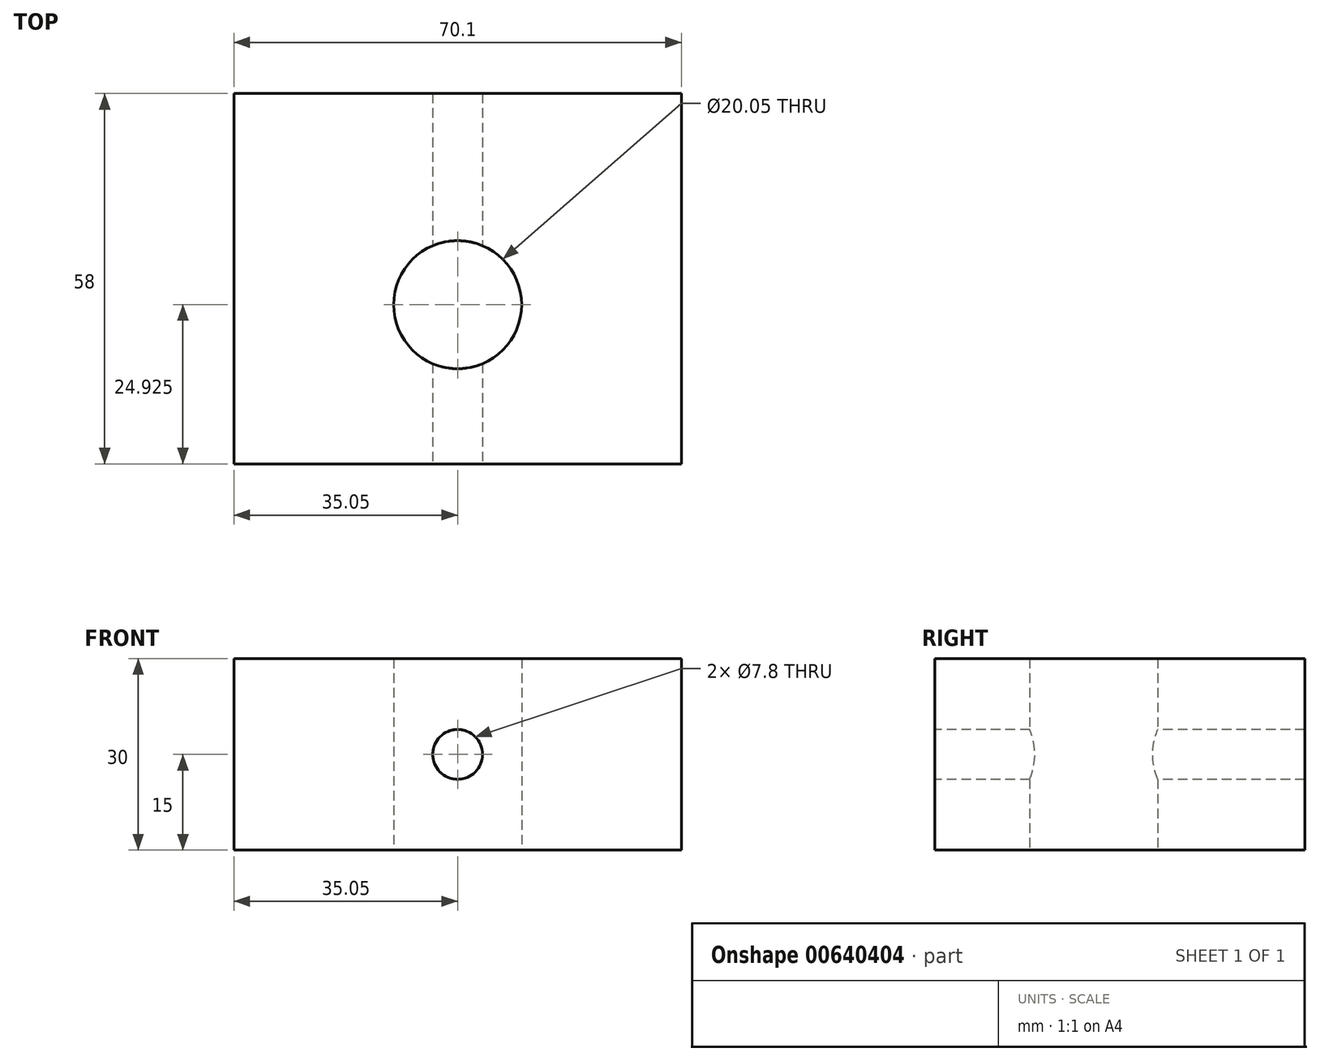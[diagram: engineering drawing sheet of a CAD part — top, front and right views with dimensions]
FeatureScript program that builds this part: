
annotation { "Feature Type Name" : "Feature", "Feature Type Description" : "" }
export const myFeature = defineFeature(function(context is Context, id is Id, definition is map)
    precondition{}
    {
        {
            var Q0;
            Q0=qCreatedBy(makeId("Top.planeOp"),FACE);
            var sketch = newSketch(context, id + "F0", { "sketchPlane" : qUnion([Q0])});
            skLineSegment(sketch, "E0.bottom", {"start": v(0, 0) * mm, "end": v(70.1, 0) * mm});
            skLineSegment(sketch, "E0.top", {"start": v(0, -58) * mm, "end": v(70.1, -58) * mm});
            skLineSegment(sketch, "E0.left", {"start": v(0, 0) * mm, "end": v(0, -58) * mm});
            skLineSegment(sketch, "E0.right", {"start": v(70.1, 0) * mm, "end": v(70.1, -58) * mm});
            skLineSegment(sketch, "E1", {"start": v(70.1, -33.15) * mm, "end": v(53.9, -33.15) * mm, "construction": true});
            skLineSegment(sketch, "E2", {"start": v(53.9, -33.15) * mm, "end": v(53.9, -50.8) * mm, "construction": true});
            skLineSegment(sketch, "E3", {"start": v(0, -33.15) * mm, "end": v(16.2, -33.15) * mm, "construction": true});
            skLineSegment(sketch, "E4", {"start": v(16.2, -33.15) * mm, "end": v(16.2, -50.8) * mm, "construction": true});
            skLineSegment(sketch, "E5", {"start": v(16.2, -50.8) * mm, "end": v(53.9, -50.8) * mm, "construction": true});
            skLineSegment(sketch, "E6", {"start": v(35.05, -33.15) * mm, "end": v(35.05, -15.1) * mm, "construction": true});
            skLineSegment(sketch, "E7", {"start": v(35.05, -33.15) * mm, "end": v(35.05, -50.8) * mm, "construction": true});
            skSolve(sketch);
        }
        {
            var Q0;
            Q0 = qSketchRegion(id + "F0", true);
            extrude(context, id + "F1", {"entities" : qUnion([Q0]), "depth" : 30 * mm, "offsetDistance" : 25 * mm});
        }
        {
            var Q0;
            {var subQ3=sQuery(id+"F0.wireOp",EDGE,"E0.bottom");Q0=makeQuery(id+"F0.imprint","IMPRINT",FACE,{"disambiguationData":[TD([[makeQuery(id+"F0.imprint","IMPRINT",EDGE,{"derivedFrom":subQ3}),-1.0]])]});}
            var sketch = newSketch(context, id + "F2", { "sketchPlane" : qUnion([Q0])});
            skLineSegment(sketch, "E8", {"start": v(0, -33.07) * mm, "end": v(16.2, -33.07) * mm, "construction": true});
            skLineSegment(sketch, "E9", {"start": v(16.2, -33.07) * mm, "end": v(16.2, -50.72) * mm, "construction": true});
            skLineSegment(sketch, "E10", {"start": v(70.1, -33.07) * mm, "end": v(70.1, -57.92) * mm, "construction": true});
            skLineSegment(sketch, "E11", {"start": v(70.1, -33.07) * mm, "end": v(53.9, -33.07) * mm, "construction": true});
            skLineSegment(sketch, "E12", {"start": v(53.9, -33.07) * mm, "end": v(53.9, -15.02) * mm, "construction": true});
            skLineSegment(sketch, "E13", {"start": v(53.9, -33.07) * mm, "end": v(16.2, -33.07) * mm, "construction": true});
            skLineSegment(sketch, "E14", {"start": v(35.05, -15.02) * mm, "end": v(35.05, -50.72) * mm, "construction": true});
            skPoint(sketch, "E14.startSnap0", {"position": v(35.05, -33.07) * mm});
            skCircle(sketch, "E15", {"center": v(35.05, -33.07) * mm, "radius": 10.03 * mm});
            skSolve(sketch);
        }
        {
            var Q0;
            Q0 = qSketchRegion(id + "F2", true);
            extrude(context, id + "F3", {"entities" : qUnion([Q0]), "operationType" : NewBodyOperationType.REMOVE, "depth" : 30 * mm, "offsetDistance" : 25 * mm});
        }
        {
            var Q0;
            Q0=makeQuery(id+"F1.opExtrude","SWEPT_FACE",FACE,{"disambiguationData":[OSD([sQuery(id+"F0.wireOp",EDGE,"E0.top")])]});
            var sketch = newSketch(context, id + "F4", { "sketchPlane" : qUnion([Q0])});
            skLineSegment(sketch, "E16", {"start": v(0, 15) * mm, "end": v(70.1, 15) * mm, "construction": true});
            skLineSegment(sketch, "E17", {"start": v(35.05, 30) * mm, "end": v(35.05, 0) * mm, "construction": true});
            skPoint(sketch, "E18", {"position": v(35.05, 15) * mm});
            skSolve(sketch);
        }
        {
            var Q0;
            Q0=sQuery(id+"F4.wireOp",VERTEX,"E18");
            var Q1;
            Q1=makeQuery(id+"F1.opExtrude","SWEPT_BODY",BODY,{"disambiguationData":[OSD([sQuery(id+"F0.wireOp",EDGE,"E0.bottom"),sQuery(id+"F0.wireOp",EDGE,"E0.top"),sQuery(id+"F0.wireOp",EDGE,"E0.left"),sQuery(id+"F0.wireOp",EDGE,"E0.right")])]});
            hole(context, id + "F5", {"style" : HoleStyle.SIMPLE, "endStyle" : HoleEndStyle.THROUGH, "standardTappedOrClearance" : lookupTablePath({ "standard" : "ISO", "size" : "7.8", "type" : "Drilled" }), "standardBlindInLast" : lookupTablePath({ "standard" : "ISO", "size" : "7.8", "type" : "Drilled" }), "holeDiameter" : 7.8 * mm, "majorDiameter" : 5 * mm, "isTappedThrough" : true, "tappedDepth" : 12 * mm, "tapClearance" : 3, "locations" : qUnion([Q0]), "scope" : qUnion([Q1])});
        }
    });
